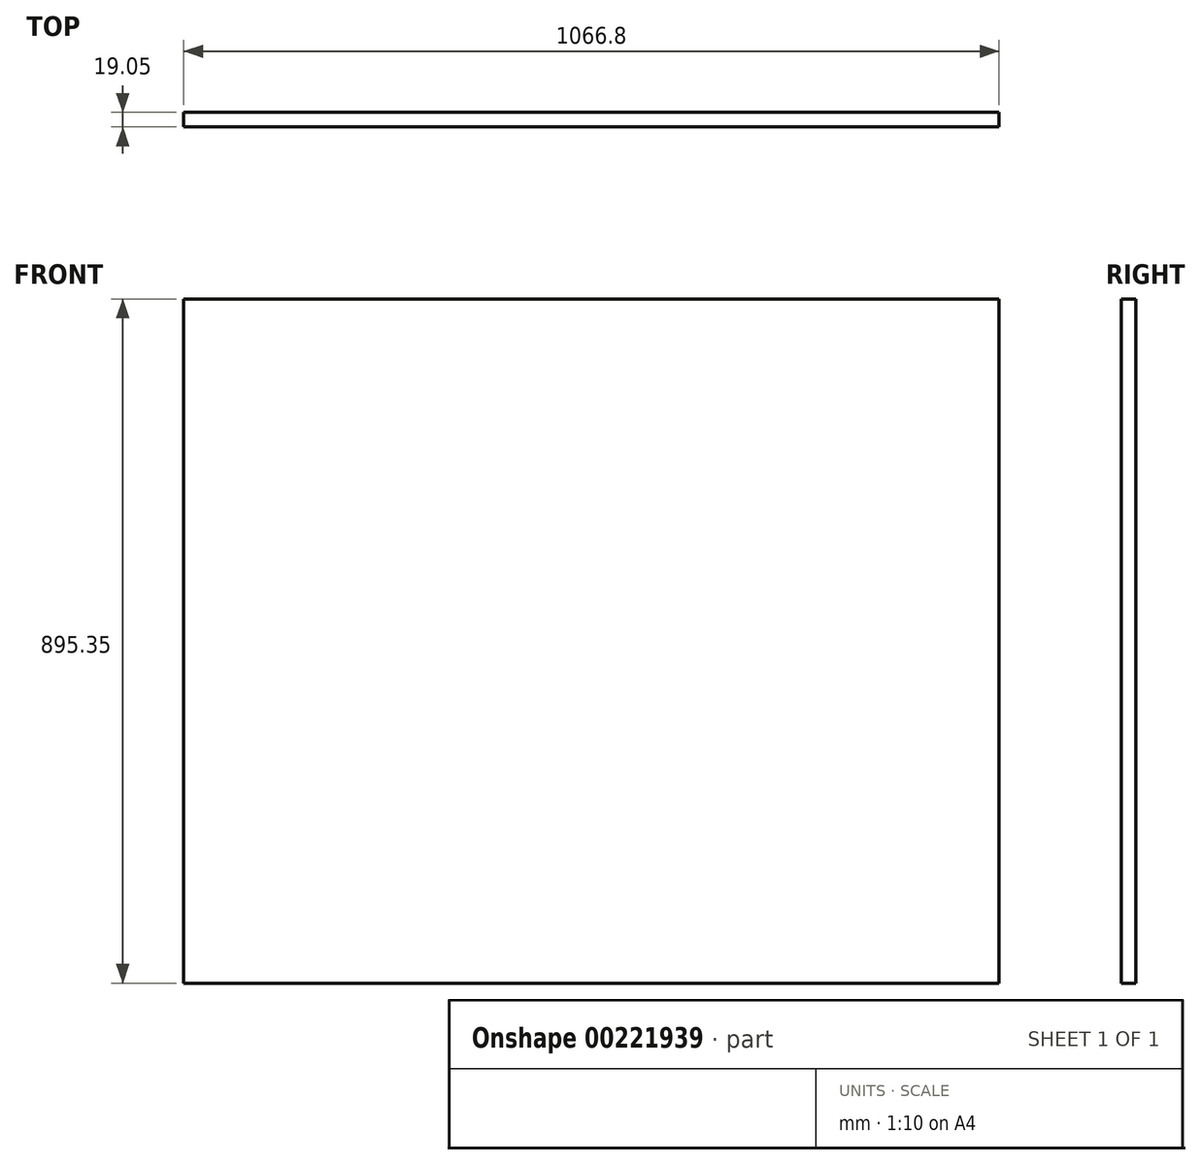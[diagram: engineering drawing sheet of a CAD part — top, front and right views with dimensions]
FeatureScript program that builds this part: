
annotation { "Feature Type Name" : "Feature", "Feature Type Description" : "" }
export const myFeature = defineFeature(function(context is Context, id is Id, definition is map)
    precondition{}
    {
        {
            var Q0;
            Q0=qCreatedBy(makeId("Front.planeOp"),FACE);
            var sketch = newSketch(context, id + "F0", { "sketchPlane" : qUnion([Q0])});
            skLineSegment(sketch, "E0.bottom", {"start": v(-473.92, 505.16) * mm, "end": v(592.88, 505.16) * mm});
            skLineSegment(sketch, "E0.top", {"start": v(-473.92, -390.2) * mm, "end": v(592.88, -390.2) * mm});
            skLineSegment(sketch, "E0.left", {"start": v(-473.92, 505.16) * mm, "end": v(-473.92, -390.2) * mm});
            skLineSegment(sketch, "E0.right", {"start": v(592.88, 505.16) * mm, "end": v(592.88, -390.2) * mm});
            skSolve(sketch);
        }
        {
            var Q0;
            Q0 = qSketchRegion(id + "F0", true);
            extrude(context, id + "F1", {"entities" : qUnion([Q0]), "depth" : 19.05 * mm});
        }
    });
